# Revit family: 6926 Стальной фонарный столб Т-05-2 со светильником Хоббика
name_source: partatom
category: Антураж
revit_build: Autodesk Revit 2018 (Build: 20180423_1000(x64)
units: mm (PartAtom-declared; Revit-internal decimal feet)

## family parameters
Всегда вертикально = Да
Источник визуального образа = Геометрия семейства
На основе рабочей плоскости = Нет
Общий = Нет
При загрузке вырезать с полостями = Нет
Точка расчета площади = Нет

## types (6) — shared parameters
URL = https://hobbyka.ru
Артикул товара = Арт. 6926
Группа модели = Светильники со стальными опорами
Длина = 1307 мм
Изготовитель = ООО «Хоббика»
Изображение типоразмера = Стальной фонарный столб Т-05-2 со светильником Арт 6926.jpg
Материал изделия = Сталь
Цвет каркаса = Сталь
Ширина = 400 мм

## per-type parameters (varying)
| type | Версия 3,26 м | Версия 3,76 м | Версия 4,26 м | Версия 4,76 м | Версия 5,26 м | Высота | Описание |
| Версия 3,26 м | Да | Нет | Нет | Нет | Нет | 3260 мм | Стальной фонарный столб Т-05-2 со светильником. Модель 3,26 м |
| Версия 3,76 м | Нет | Да | Нет | Нет | Нет | 3760 мм | Стальной фонарный столб Т-05-2 со светильником. Модель 3,76 м |
| Версия 4,26 м | Нет | Нет | Да | Нет | Нет | 4260 мм | Стальной фонарный столб Т-05-2 со светильником. Модель 4,26 м |
| Версия 4,76 м | Нет | Нет | Нет | Да | Нет | 4760 мм | Стальной фонарный столб Т-05-2 со светильником. Модель 4,76 м |
| Версия 5,26 м | Нет | Нет | Нет | Нет | Да | 5260 мм | Стальной фонарный столб Т-05-2 со светильником. Модель 5,26 м |
| Версия 5,76 м | Нет | Нет | Нет | Нет | Нет | 5760 мм | Стальной фонарный столб Т-05-2 со светильником. Модель 5,76 м |
